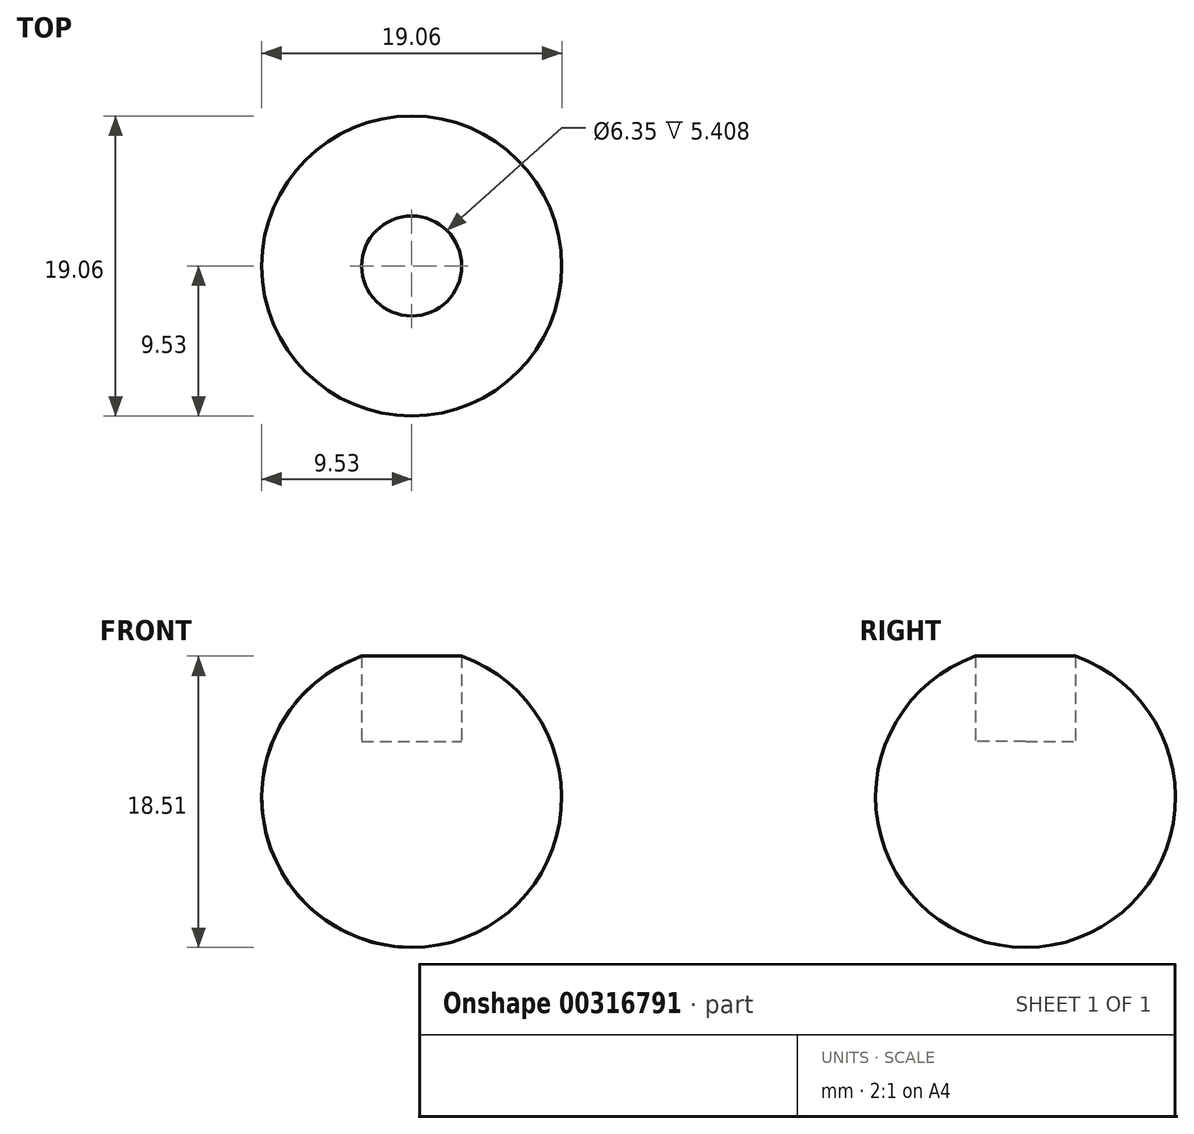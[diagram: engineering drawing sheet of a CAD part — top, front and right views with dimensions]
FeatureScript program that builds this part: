
annotation { "Feature Type Name" : "Feature", "Feature Type Description" : "" }
export const myFeature = defineFeature(function(context is Context, id is Id, definition is map)
    precondition{}
    {
        {
            var Q0;
            Q0=qCreatedBy(makeId("Front.planeOp"),FACE);
            var sketch = newSketch(context, id + "F0", { "sketchPlane" : qUnion([Q0])});
            skArc(sketch, "E0", {"start": v(0, 9.53) * mm, "mid": v(-9.53, 0) * mm, "end": v(0, -9.53) * mm});
            skLineSegment(sketch, "E1", {"start": v(0, 9.53) * mm, "end": v(0, -9.53) * mm});
            skSolve(sketch);
        }
        {
            var Q0;
            Q0=makeQuery(id+"F0.imprint","IMPRINT",FACE,{"disambiguationData":[TD([[makeQuery(id+"F0.imprint","IMPRINT",EDGE,{"derivedFrom":sQuery(id+"F0.wireOp",EDGE,"E0")}),1.0]])]});
            var Q1;
            Q1=sQuery(id+"F0.wireOp",EDGE,"E1");
            revolve(context, id + "F1", {"entities" : qUnion([Q0]), "axis" : qUnion([Q1]), "revolveType" : RevolveType.FULL});
        }
        {
            var Q0;
            Q0=qCreatedBy(makeId("Top.planeOp"),FACE);
            cPlane(context, id + "F2", {"entities" : qUnion([Q0]), "cplaneType" : CPlaneType.OFFSET, "offset" : 3.57 * mm, "width" : 152.4 * mm, "height" : 152.4 * mm});
        }
        {
            var Q0;
            Q0=qCreatedBy(id+"F2.planeOp",FACE);
            var sketch = newSketch(context, id + "F3", { "sketchPlane" : qUnion([Q0])});
            skCircle(sketch, "E2", {"center": v(0, 0) * mm, "radius": 3.18 * mm});
            skSolve(sketch);
        }
        {
            var Q0;
            Q0 = qSketchRegion(id + "F3", true);
            extrude(context, id + "F4", {"entities" : qUnion([Q0]), "operationType" : NewBodyOperationType.REMOVE, "depth" : 25.4 * mm});
        }
    });
